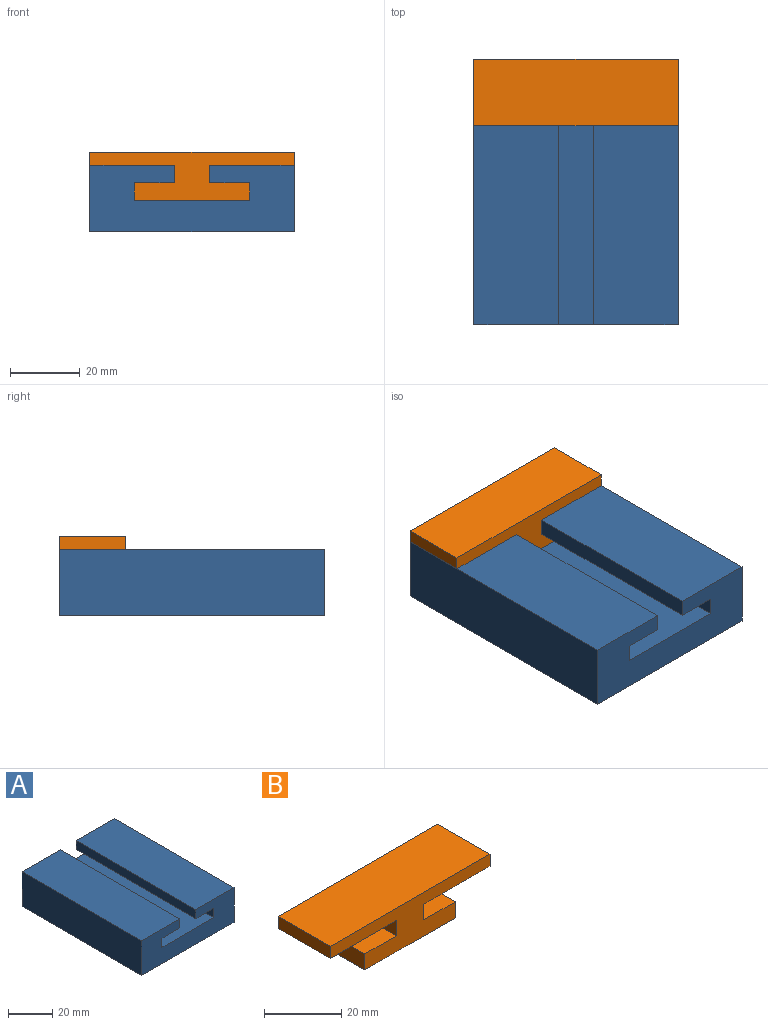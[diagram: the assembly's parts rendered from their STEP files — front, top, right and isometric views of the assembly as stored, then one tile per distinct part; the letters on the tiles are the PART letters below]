
ASSEMBLY  parts=2 mates=1
PART A: 14 faces, bbox 58.6x76.2x19.1 mm
  f0: plane 76.2x58.61mm, normal (0,0,-1), area 4465.9mm2, adj f1,f11,f12,f13
  f1: plane 76.2x19.05mm, normal (1,0,0), area 1451.6mm2, adj f0,f2,f12,f13
  f2: plane 76.2x24.22mm, normal (0,0,1), area 1845.8mm2, adj f1,f3,f12,f13
  f3: plane 76.2x4.94mm, normal (-1,0,0), area 376.1mm2, adj f2,f4,f12,f13
  f4: plane 76.2x11.43mm, normal (0,0,-1), area 871mm2, adj f3,f5,f12,f13
  f5: plane 76.2x5.08mm, normal (-1,0,0), area 387.1mm2, adj f4,f6,f12,f13
  f6: plane 76.2x33.02mm, normal (0,0,1), area 2516.1mm2, adj f5,f7,f12,f13
  f7: plane 76.2x5.08mm, normal (1,0,0), area 387.1mm2, adj f6,f8,f12,f13
  f8: plane 76.2x11.43mm, normal (0,0,-1), area 871mm2, adj f7,f9,f12,f13
  f9: plane 76.2x4.94mm, normal (1,0,0), area 376.1mm2, adj f8,f10,f12,f13
  f10: plane 76.2x24.22mm, normal (0,0,1), area 1845.8mm2, adj f9,f11,f12,f13
  f11: plane 76.2x19.05mm, normal (-1,0,0), area 1451.6mm2, adj f0,f10,f12,f13
  f12: plane 58.61x19.05mm, normal (0,-1,0), area 898.6mm2, adj f0,f1,f2,f3,f4,f5,f6,f7
  f13: plane 58.61x19.05mm, normal (0,1,0), area 898.6mm2, adj f0,f1,f2,f3,f4,f5,f6,f7
PART B: 14 faces, bbox 58.6x19.1x13.8 mm
  f0: plane 24.22x19.05mm, normal (0,0,-1), area 461.5mm2, adj f1,f11,f12,f13
  f1: plane 19.05x4.94mm, normal (-1,0,0), area 94mm2, adj f0,f2,f12,f13
  f2: plane 19.05x11.43mm, normal (0,0,1), area 217.7mm2, adj f1,f3,f12,f13
  f3: plane 19.05x5.08mm, normal (-1,0,0), area 96.8mm2, adj f2,f4,f12,f13
  f4: plane 33.02x19.05mm, normal (0,0,-1), area 629mm2, adj f3,f5,f12,f13
  f5: plane 19.05x5.08mm, normal (1,0,0), area 96.8mm2, adj f4,f6,f12,f13
  f6: plane 19.05x11.43mm, normal (0,0,1), area 217.7mm2, adj f5,f7,f12,f13
  f7: plane 19.05x4.94mm, normal (1,0,0), area 94mm2, adj f6,f8,f12,f13
  f8: plane 24.22x19.05mm, normal (0,0,-1), area 461.5mm2, adj f7,f9,f12,f13
  f9: plane 19.05x3.81mm, normal (1,0,0), area 72.6mm2, adj f8,f10,f12,f13
  f10: plane 58.61x19.05mm, normal (0,0,1), area 1116.5mm2, adj f9,f11,f12,f13
  f11: plane 19.05x3.81mm, normal (-1,0,0), area 72.6mm2, adj f0,f10,f12,f13
  f12: plane 58.61x13.83mm, normal (0,-1,0), area 441.2mm2, adj f0,f1,f2,f3,f4,f5,f6,f7
  f13: plane 58.61x13.83mm, normal (0,1,0), area 441.2mm2, adj f0,f1,f2,f3,f4,f5,f6,f7
PLACE A t=(0,50.26,0)mm fixed
PLACE B t=(0,50.26,0)mm
MATE slider B.f13 <-> A.f13  axis (0,1,0) through (-16.51,50.26,9.03)mm
